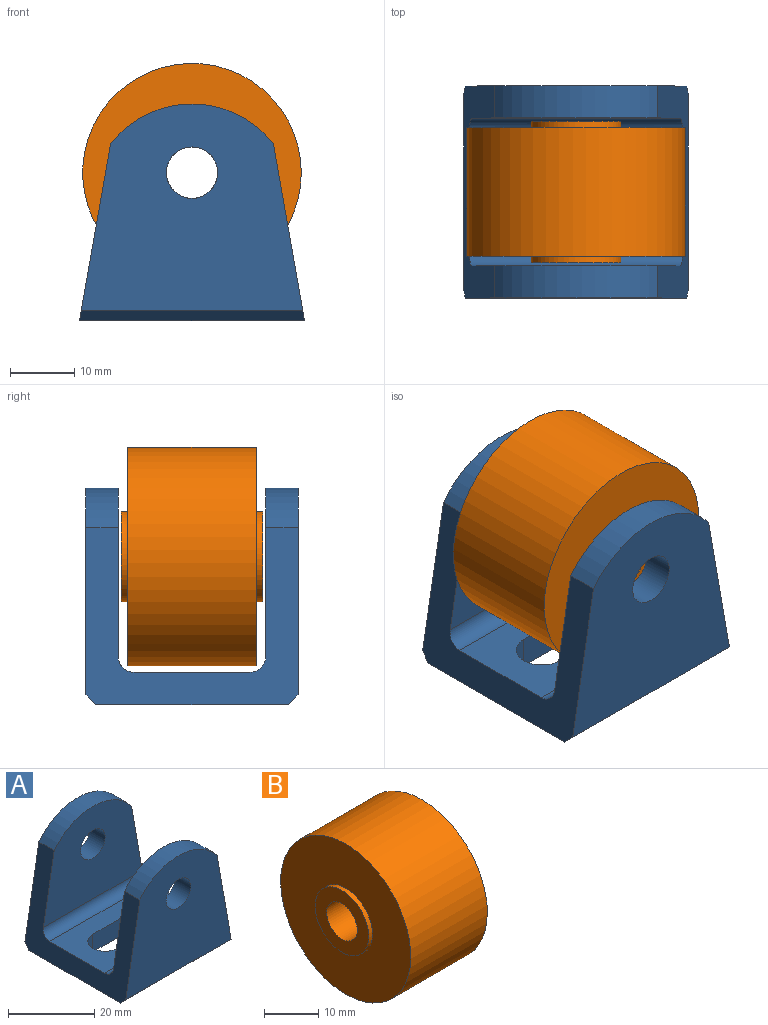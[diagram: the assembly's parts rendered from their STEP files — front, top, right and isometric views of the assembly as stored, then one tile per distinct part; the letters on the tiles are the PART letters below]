
ASSEMBLY  parts=2 mates=1
PART A: 20 faces, bbox 35x33x33.7 mm
  f0: plane 35x30mm, normal (0,0,-1), area 879.7mm2, adj f2,f3,f12,f13,f16,f17,f18,f19
  f1: plane 33.24x18mm, normal (0,0,1), area 428mm2, adj f2,f3,f8,f9,f16,f17,f18,f19
  f2: plane 33x27.5mm, normal (-0.98,0,0.17), area 396.5mm2, adj f0,f1,f4,f5,f6,f7,f8,f9
  f3: plane 33x27.5mm, normal (0.98,0,0.17), area 396.5mm2, adj f0,f1,f4,f5,f6,f7,f8,f9
  f4: cylinder r=16mm len=25.3mm, axis (0,1,0), area 145.9mm2, adj f2,f3,f6,f11
  f5: cylinder r=16mm len=25.3mm, axis (0,1,0), area 145.9mm2, adj f2,f3,f7,f10
  f6: plane 34.47x32.2mm, normal (0,-1,0), area 836.3mm2, adj f2,f3,f4,f12,f14
  f7: plane 34.47x32.2mm, normal (0,1,0), area 836.3mm2, adj f2,f3,f5,f13,f15
  f8: cylinder r=2.5mm len=33.24mm, axis (-1,0,0), area 129.3mm2, adj f1,f2,f3,f11
  f9: cylinder r=2.5mm len=33.24mm, axis (-1,0,0), area 129.3mm2, adj f1,f2,f3,f10
  f10: plane 32.36x26.2mm, normal (0,-1,0), area 635.8mm2, adj f2,f3,f5,f9,f15
  f11: plane 32.36x26.2mm, normal (0,1,0), area 635.8mm2, adj f2,f3,f4,f8,f14
  f12: plane 35x1.5mm, normal (0,-0.71,-0.71), area 73.7mm2, adj f0,f2,f3,f6
  f13: plane 35x1.5mm, normal (0,0.71,-0.71), area 73.7mm2, adj f0,f2,f3,f7
  f14: cylinder r=4mm len=8mm, axis (0,1,0), area 125.7mm2, adj f6,f11
  f15: cylinder r=4mm len=8mm, axis (0,1,0), area 125.7mm2, adj f7,f10
  f16: plane 15x5mm, normal (0,-1,0), area 75mm2, adj f0,f1,f17,f19
  f17: cylinder r=4mm len=8mm, axis (0,0,1), area 62.8mm2, adj f0,f1,f16,f18
  f18: plane 15x5mm, normal (0,1,0), area 75mm2, adj f0,f1,f17,f19
  f19: cylinder r=4mm len=8mm, axis (0,0,1), area 62.8mm2, adj f0,f1,f16,f18
PART B: 8 faces, bbox 22x34x34 mm
  f0: cylinder r=4mm len=22mm, axis (-1,0,0), area 552.9mm2, adj f1,f7
  f1: plane 14x14mm, normal (1,0,0), area 103.7mm2, adj f0,f2
  f2: cylinder r=7mm len=14mm, axis (-1,0,0), area 44mm2, adj f1,f3
  f3: plane 34x34mm, normal (1,0,0), area 754mm2, adj f2,f4
  f4: cylinder r=17mm len=34mm, axis (-1,0,0), area 2136.3mm2, adj f3,f5
  f5: plane 34x34mm, normal (-1,0,0), area 754mm2, adj f4,f6
  f6: cylinder r=7mm len=14mm, axis (-1,0,0), area 44mm2, adj f5,f7
  f7: plane 14x14mm, normal (-1,0,0), area 103.7mm2, adj f0,f6
PLACE A t=(-6.57,7.7,-0.88)mm
PLACE B rot(axis=(0.58,0.58,0.58),120deg) t=(-6.57,7.7,22.12)mm
MATE slider B.f0 <-> A.f14  axis (0,1,0) through (-6.57,18.7,22.12)mm
